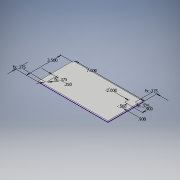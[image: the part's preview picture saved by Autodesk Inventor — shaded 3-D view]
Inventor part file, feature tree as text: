
AUTODESK INVENTOR PART (.ipt)
format: ipt  version: 2018 (Build 220112000, 112)  size: 115,200 bytes
history: native  units: in
note: dims shown in document units (in); Inventor stores cm internally (conversion verified against a paired STEP export)
features: sketch x2, extrude x2
ambient origin geometry x8: Origin, YZ Plane, XZ Plane, XY Plane, X Axis, Y Axis, Z Axis, Center Point
bodies: Solid1 (feature_tree)
feature tree (4):
  sketch  "Sketch1"  dims[d0=7.0in d1=3.5in]
  extrude  "Extrusion1"  Depth=3.5in
  extrude  "Extrusion2"  Depth=0.9in
  sketch  "Sketch2"  dims[d2=0.9in d3=0.9in d4=0.5in d5=2.0in d6=0.125in d7=0.0in d8=0.6in d9=0.0in d10=0.375in d11=0.375in d12=0.375in d13=0.375in d14=0.25in d15=0.375in d16=0.375in]
